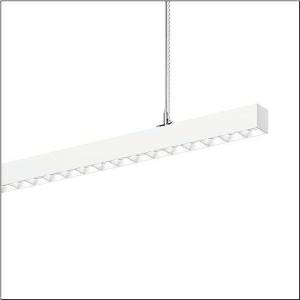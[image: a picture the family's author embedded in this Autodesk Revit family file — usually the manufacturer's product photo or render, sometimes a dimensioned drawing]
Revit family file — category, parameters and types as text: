
# Revit family: silica_21_51mx36dc4dwb
name_source: partatom
category: Lighting Fixtures
units: mm (PartAtom-declared; Revit-internal decimal feet)

## family parameters
Cut with Voids When Loaded = No
Host = Face
Light Source = No
Part Type = Normal
Room Calculation Point = No
Round Connector Dimension = Use Diameter
Shared = No

## types (1)
- --- (1 x LED, 17650 lm, 97.4 W, 4000K)
    Apparent Load = 97 VA
    CIE Flux Codes = 83 98 100 61 100
    Color Rendering = 80
    Color Temperature = 4000K
    Default Elevation = 1800 mm
    Description = Silica 21, office luminaire, primary light control with darklight reflector, of PMMA, white, CAT 2 (L<= 3000cd/m²), light emission: direct/indirect distribution, primary light characteristic: symmetric, installation type: suspended mounting, LED, rated luminous flux: 17.650lm, luminous efficacy: 181lm/W, light colour: 840, colour temperature: 4000K, control gear: DALI 2, with terminal, 3+2-pole, max. 2.5mm², mains connection: 220..240V, AC, 50/60Hz, rated input power: 97.4W, luminaire housing, of aluminium, traffic white (RAL 9016), length: 3.004mm, width: 53mm, height: 53mm, protection rating (complete): IP20, insulation class (complete): insulation class I (protective earthing), certification: CE, permissible operating ambient temperature: 0..+35°C, standard: EN 50419, packaging unit: 1 piece
    Height = 53 mm
    Lamp = 1 x LED
    Lamp Light Flux = 17650 lm
    Lamp Power = 97.4 W
    Lamp count = 1
    Length = 3004 mm
    Luminous efficacy = 181 lm/W
    Manufacturer = Siteco
    ModVariant = No
    Model = 51MX36DC4DWB
    Mounting Place = Ceiling
    Mounting Type = Pendant
    Number of Poles = 1
    OnlyDefault = Yes
    Power Factor = 1
    Product Name = Silica 21
    Product group = office luminaire | ceiling pendant
    ProductGroupID = 903
    Protection Class = Protection class I
    Protection Degree = IP 20
    RLX_Detail_Level = 1
    RLX_Emergency_Light_Flux = 0 lm
    RLX_Emergency_Type = 0
    RLX_Emergency_Type_DB = No
    RlxData = <blob elided: 61621 chars, md5=ed3b8378>
    Socket = socket
    Standby Power = 0 W
    System Light Flux = 17650 lm
    System Power = 97 W
    Type Comments = factory setting: luminous flux: 100 % | dim-lin: 254 | 336 mA
    Type Image = l_1335921.jpg
    URL = http://relux.com
    VarID = @adj_121647
    Voltage = 0 V
    Weight = 0.00 kg
    Width = 53 mm

## geometry (parser evidence)
native form markers: Blend x4, Sweep x13
no freeform markers — native parametric forms only
